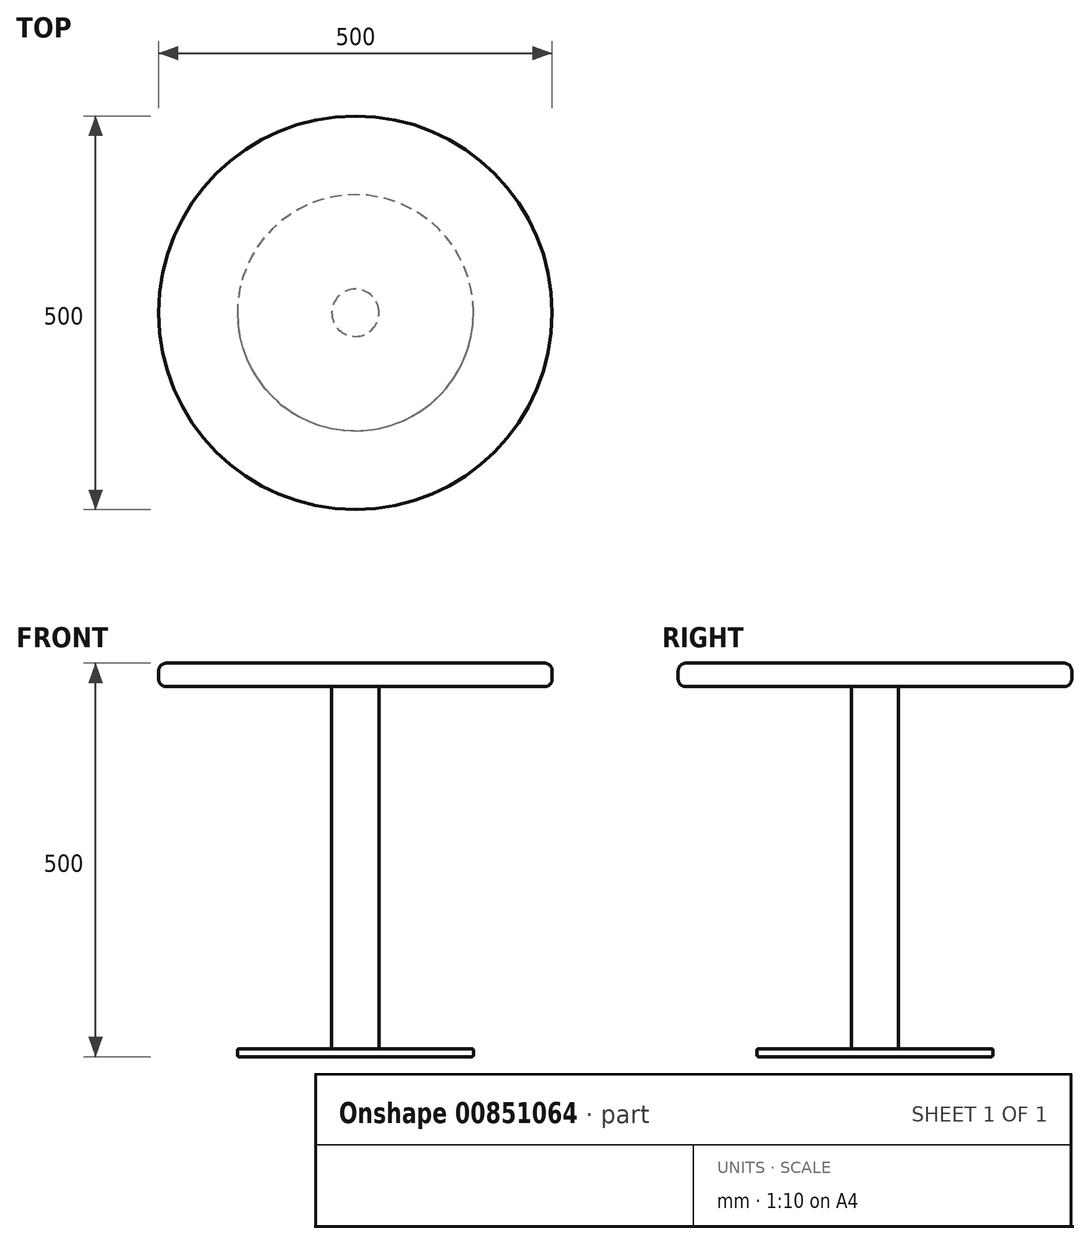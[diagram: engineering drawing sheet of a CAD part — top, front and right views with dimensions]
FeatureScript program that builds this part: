
annotation { "Feature Type Name" : "Feature", "Feature Type Description" : "" }
export const myFeature = defineFeature(function(context is Context, id is Id, definition is map)
    precondition{}
    {
        {
            var Q0;
            Q0=qCreatedBy(makeId("Front.planeOp"),FACE);
            var sketch = newSketch(context, id + "F0", { "sketchPlane" : qUnion([Q0])});
            skLineSegment(sketch, "E0", {"start": v(0, 0) * mm, "end": v(-150, 0) * mm});
            skLineSegment(sketch, "E1", {"start": v(-150, 0) * mm, "end": v(-150, 10) * mm});
            skLineSegment(sketch, "E2", {"start": v(-150, 10) * mm, "end": v(-30, 10) * mm});
            skLineSegment(sketch, "E3", {"start": v(-30, 10) * mm, "end": v(-30, 470) * mm});
            skLineSegment(sketch, "E4", {"start": v(-30, 470) * mm, "end": v(-250, 470) * mm});
            skLineSegment(sketch, "E5", {"start": v(-250, 470) * mm, "end": v(-250, 500) * mm});
            skLineSegment(sketch, "E6", {"start": v(-250, 500) * mm, "end": v(0, 500) * mm});
            skLineSegment(sketch, "E7", {"start": v(0, 500) * mm, "end": v(0, 0) * mm});
            skSolve(sketch);
        }
        {
            var Q0;
            Q0=makeQuery(id+"F0.imprint","IMPRINT",FACE,{"disambiguationData":[TD([[makeQuery(id+"F0.imprint","IMPRINT",EDGE,{"derivedFrom":sQuery(id+"F0.wireOp",EDGE,"E0")}),-1.0]])]});
            var Q1;
            Q1=sQuery(id+"F0.wireOp",EDGE,"E7");
            revolve(context, id + "F1", {"surfaceOperationType" : NewSurfaceOperationType.NEW, "entities" : qUnion([Q0]), "axis" : qUnion([Q1]), "revolveType" : RevolveType.FULL});
        }
        {
            var Q0;
            Q0=makeQuery(id+"F1.opRevolve","SWEPT_EDGE",EDGE,{"disambiguationData":[OSD([sQuery(id+"F0.wireOp",EDGE,"E5"),sQuery(id+"F0.wireOp",EDGE,"E6")])]});
            var Q1;
            Q1=makeQuery(id+"F1.opRevolve","SWEPT_EDGE",EDGE,{"disambiguationData":[OSD([sQuery(id+"F0.wireOp",EDGE,"E4"),sQuery(id+"F0.wireOp",EDGE,"E5")])]});
            fillet(context, id + "F2", {"entities" : qUnion([Q0, Q1]), "radius" : 10 * mm, "tangentPropagation" : true, "allowEdgeOverflow" : false});
        }
        {
            var Q0;
            Q0=makeQuery(id+"F1.opRevolve","SWEPT_EDGE",EDGE,{"disambiguationData":[OSD([sQuery(id+"F0.wireOp",EDGE,"E0"),sQuery(id+"F0.wireOp",EDGE,"E1")])]});
            var Q1;
            Q1=makeQuery(id+"F1.opRevolve","SWEPT_EDGE",EDGE,{"disambiguationData":[OSD([sQuery(id+"F0.wireOp",EDGE,"E1"),sQuery(id+"F0.wireOp",EDGE,"E2")])]});
            fillet(context, id + "F3", {"entities" : qUnion([Q0, Q1]), "radius" : 2 * mm, "tangentPropagation" : true, "allowEdgeOverflow" : false});
        }
    });
